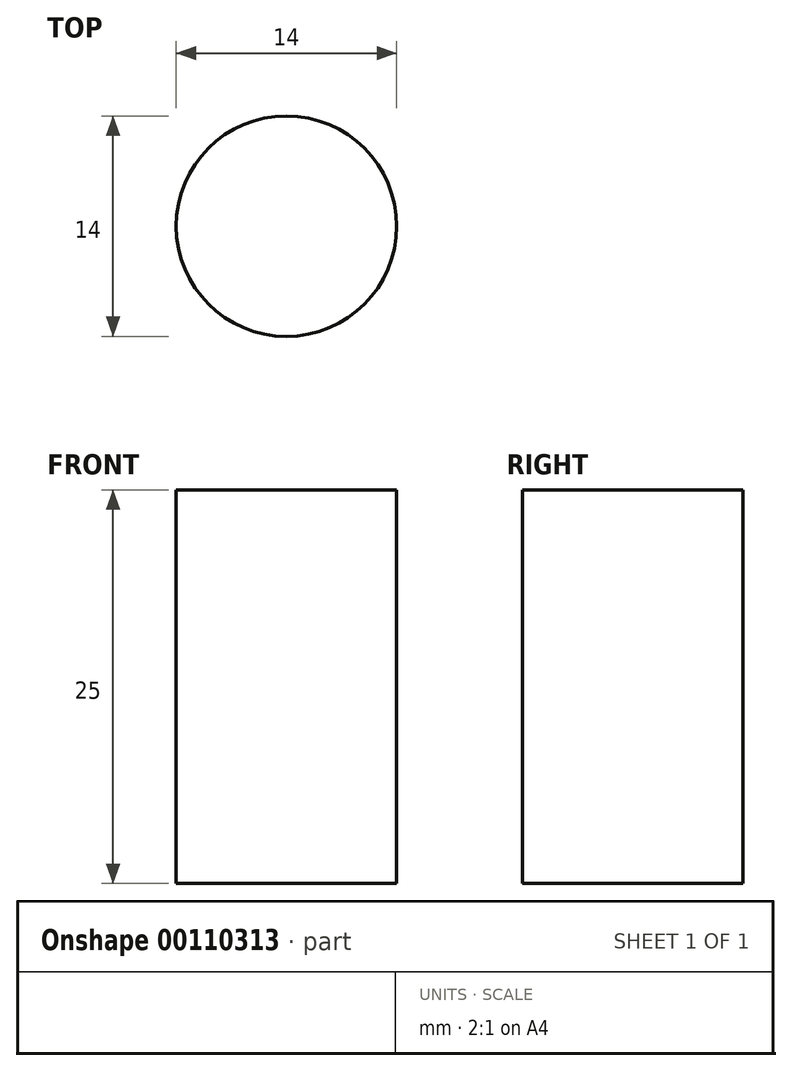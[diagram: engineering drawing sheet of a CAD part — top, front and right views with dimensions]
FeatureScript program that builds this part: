
annotation { "Feature Type Name" : "Feature", "Feature Type Description" : "" }
export const myFeature = defineFeature(function(context is Context, id is Id, definition is map)
    precondition{}
    {
        {
            var Q0;
            Q0=qCreatedBy(makeId("Top.planeOp"), FACE);
            var sketch = newSketch(context, id + "F0", { "sketchPlane" : qUnion([Q0])});
            skCircle(sketch, "E0", {"center": v(0, 0) * mm, "radius": 7 * mm});
            skSolve(sketch);
        }
        {
            var Q0;
            Q0 = qSketchRegion(id + "F0", true);
            extrude(context, id + "F1", {"entities" : qUnion([Q0]), "depth" : 25 * mm, "offsetDistance" : 25 * mm});
        }
    });
